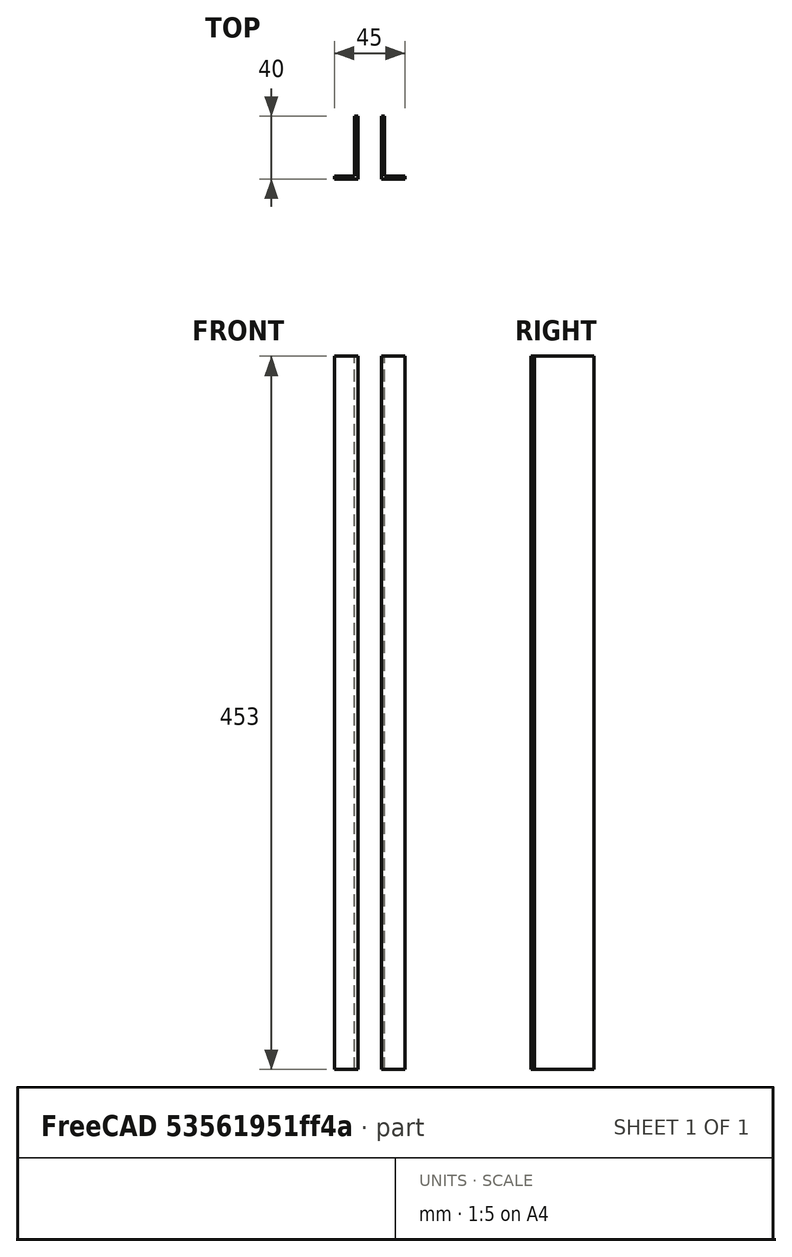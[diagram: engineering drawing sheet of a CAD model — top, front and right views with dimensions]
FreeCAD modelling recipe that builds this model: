
FCSTD DOCUMENT  (FreeCAD 0.16R6698 (Git))
Label: u
License: All rights reserved
LicenseURL: http://en.wikipedia.org/wiki/All_rights_reserved
objects: Sketcher::SketchObject×1, PartDesign::Pad×1
note: 3 computed .brp shape members not serialized (recipe doc carries the construction recipe); baked Part::Feature solids carry a one-line shape summary decoded from their .brp

FEATURE [Sketcher::SketchObject] Sketch
  sketch-geometry (12):
    g0: LineSegment StartX=-9.5 StartY=38 StartZ=0 EndX=-7.5 EndY=38 EndZ=0
    g1: LineSegment StartX=-7.5 StartY=38 StartZ=0 EndX=-7.5 EndY=-2 EndZ=0
    g2: LineSegment StartX=7.5 StartY=-2 StartZ=0 EndX=7.5 EndY=38 EndZ=0
    g3: LineSegment StartX=7.5 StartY=38 StartZ=0 EndX=9.5 EndY=38 EndZ=0
    g4: LineSegment StartX=9.5 StartY=38 StartZ=0 EndX=9.5 EndY=0 EndZ=0
    g5: LineSegment StartX=-9.5 StartY=0 StartZ=0 EndX=-9.5 EndY=38 EndZ=0
    g6: LineSegment StartX=7.5 StartY=-2 StartZ=0 EndX=22.5 EndY=-2 EndZ=0
    g7: LineSegment StartX=9.5 StartY=0 StartZ=0 EndX=22.5 EndY=0 EndZ=0
    g8: LineSegment StartX=22.5 StartY=0 StartZ=0 EndX=22.5 EndY=-2 EndZ=0
    g9: LineSegment StartX=-7.5 StartY=-2 StartZ=0 EndX=-22.5 EndY=-2 EndZ=0
    g10: LineSegment StartX=-22.5 StartY=-2 StartZ=0 EndX=-22.5 EndY=0 EndZ=0
    g11: LineSegment StartX=-22.5 StartY=0 StartZ=0 EndX=-9.5 EndY=0 EndZ=0
  constraints (36):
    c: Horizontal(g0)
    c: Coincident(g0,g1)
    c: Vertical(g1)
    c: Vertical(g2)
    c: Coincident(g2,g3)
    c: Horizontal(g3)
    c: Coincident(g3,g4)
    c: Vertical(g4)
    c: Coincident(g5,g0)
    c: Vertical(g5)
    c: DistanceY(g5,g5) = 38
    c: DistanceY(g4,g4) = 38
    c: DistanceY(g1,g1) = 40
    c: DistanceX(g3,g3) = 2
    c: DistanceX(g0,g0) = 2
    c: DistanceX(g5,g4) = 19
    c: DistanceX(g-1,g4) = 9.5
    c: DistanceY(g5,g-1) = 0
    c: DistanceY(g2,g2) = 40
    c: Coincident(g2,g6)
    c: Horizontal(g6)
    c: DistanceX(g6,g6) = 15
    c: Coincident(g4,g7)
    c: Horizontal(g7)
    c: Coincident(g7,g8)
    c: Coincident(g8,g6)
    c: Vertical(g8)
    c: Coincident(g1,g9)
    c: Horizontal(g9)
    c: Coincident(g9,g10)
    c: Vertical(g10)
    c: Coincident(g10,g11)
    c: Coincident(g11,g5)
    c: Horizontal(g11)
    c: DistanceX(g11,g11) = 13
    c: DistanceY(g1,g2) = 0
FEATURE [PartDesign::Pad] Pad
  Length = 453
  Length2 = 100
  Sketch = -> Sketch
  Type = 0
